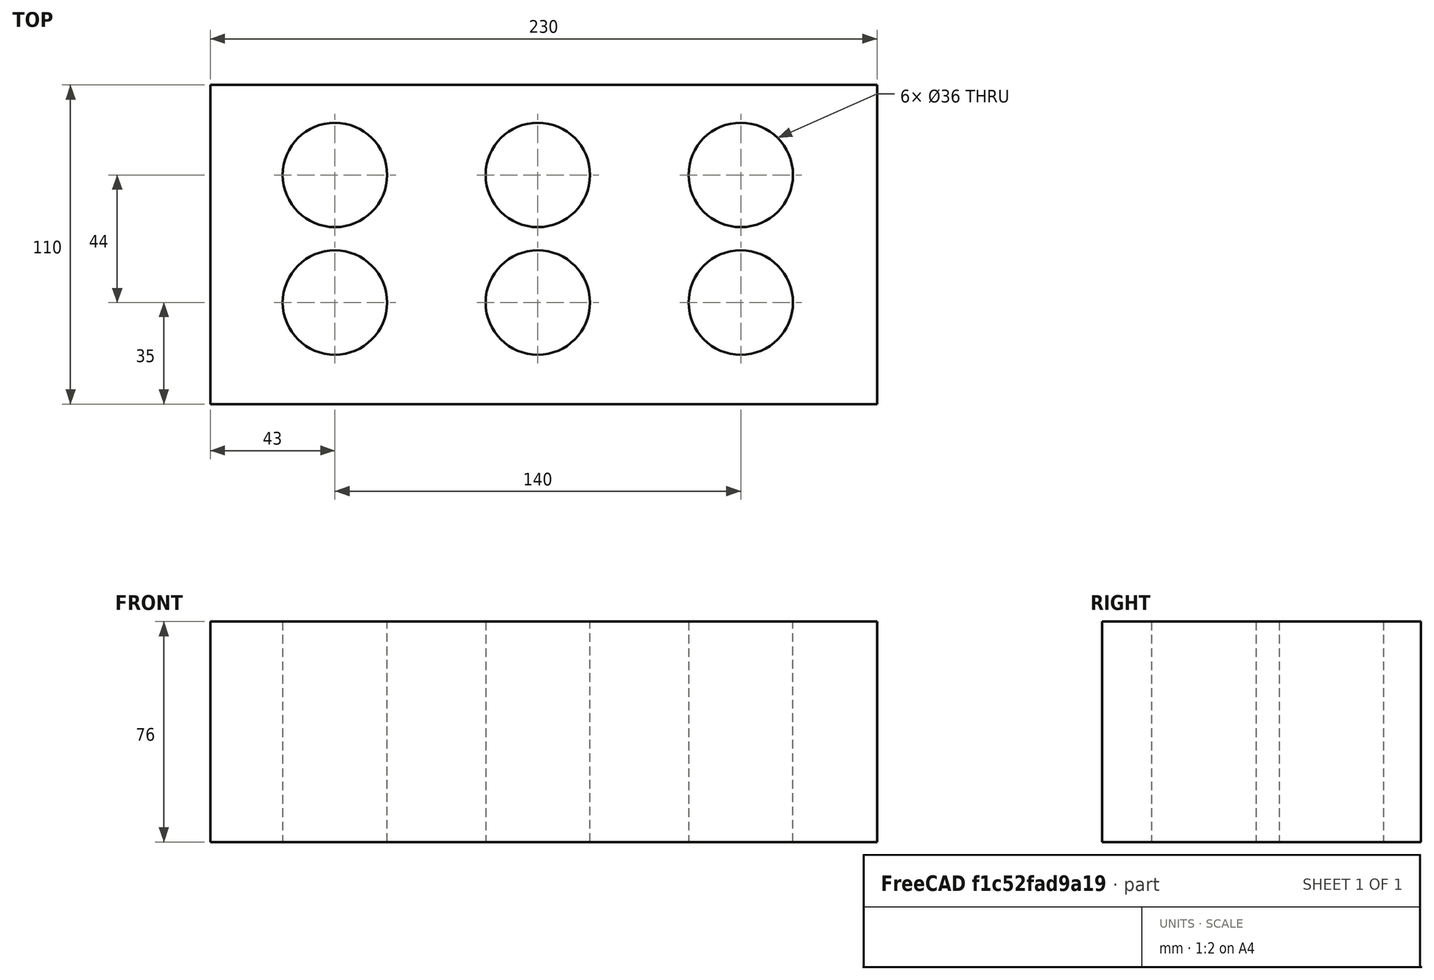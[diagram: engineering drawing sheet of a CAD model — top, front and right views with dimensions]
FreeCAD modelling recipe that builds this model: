
FCSTD DOCUMENT  (FreeCAD 1.0R39319 (Git))
Label: ojt1_t09r02_birck
License: All rights reserved
LicenseURL: https://en.wikipedia.org/wiki/All_rights_reserved
objects: Part::Cylinder×6, Part::Box×1, Part::MultiFuse×1, Part::Cut×1
note: 9 computed .brp shape members not serialized (recipe doc carries the construction recipe); baked Part::Feature solids carry a one-line shape summary decoded from their .brp

FEATURE [Part::Box] Box  label="Cub"
  AttacherType = Attacher::AttachEngine3D
  Height = 76
  Length = 230
  Width = 110
FEATURE [Part::Cylinder] Cylinder  label="Cilindre"
  Angle = 360
  AttacherType = Attacher::AttachEngine3D
  FirstAngle = 0
  Height = 76
  Placement = pos=(43,79,0) rot=(0,0,1;0rad)
  Radius = 18
  SecondAngle = 0
FEATURE [Part::Cylinder] Cylinder001  label="Cilindre001"
  Angle = 360
  AttacherType = Attacher::AttachEngine3D
  FirstAngle = 0
  Height = 76
  Placement = pos=(113,79,0) rot=(0,0,1;0rad)
  Radius = 18
  SecondAngle = 0
FEATURE [Part::Cylinder] Cylinder002  label="Cilindre002"
  Angle = 360
  AttacherType = Attacher::AttachEngine3D
  FirstAngle = 0
  Height = 76
  Placement = pos=(183,79,0) rot=(0,0,1;0rad)
  Radius = 18
  SecondAngle = 0
FEATURE [Part::Cylinder] Cylinder003  label="Cilindre003"
  Angle = 360
  AttacherType = Attacher::AttachEngine3D
  FirstAngle = 0
  Height = 76
  Placement = pos=(43,35,0) rot=(0,0,1;0rad)
  Radius = 18
  SecondAngle = 0
FEATURE [Part::Cylinder] Cylinder004  label="Cilindre004"
  Angle = 360
  AttacherType = Attacher::AttachEngine3D
  FirstAngle = 0
  Height = 76
  Placement = pos=(113,35,0) rot=(0,0,1;0rad)
  Radius = 18
  SecondAngle = 0
FEATURE [Part::Cylinder] Cylinder005  label="Cilindre005"
  Angle = 360
  AttacherType = Attacher::AttachEngine3D
  FirstAngle = 0
  Height = 76
  Placement = pos=(183,35,0) rot=(0,0,1;0rad)
  Radius = 18
  SecondAngle = 0
FEATURE [Part::MultiFuse] Fusion
  Refine = true
  Shapes = -> [Cylinder,Cylinder001,Cylinder002,Cylinder003,Cylinder004,Cylinder005]
FEATURE [Part::Cut] Cut
  Base = -> Box
  Refine = true
  Tool = -> Fusion
